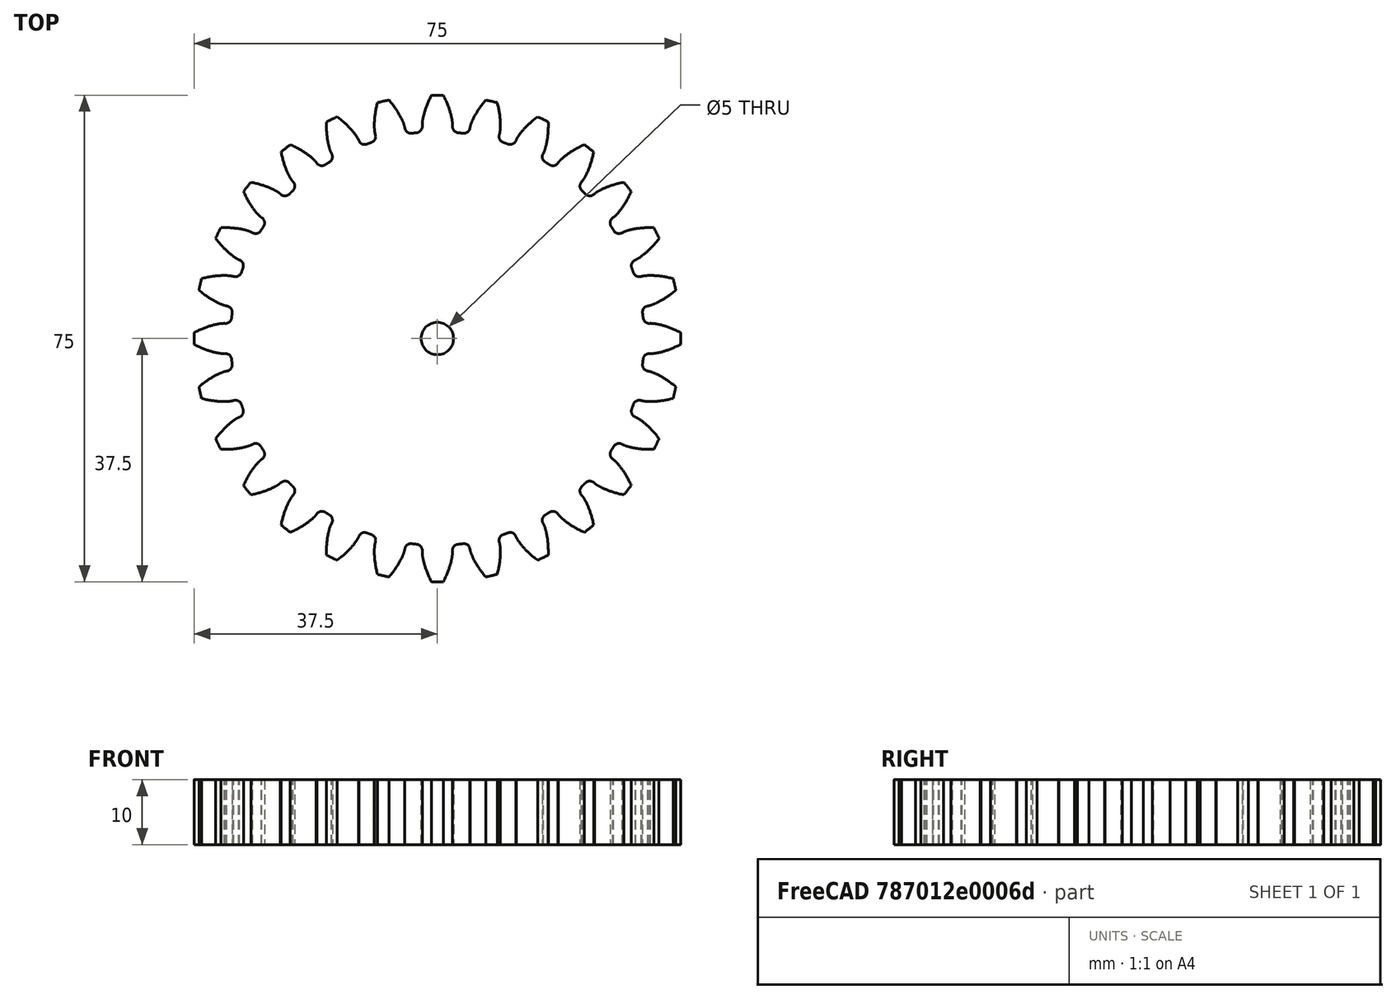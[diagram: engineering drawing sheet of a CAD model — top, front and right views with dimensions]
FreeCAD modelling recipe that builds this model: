
FCSTD DOCUMENT  (FreeCAD 1.0R39109 (Git))
Label: ギヤ70mm
License: All rights reserved
LicenseURL: https://en.wikipedia.org/wiki/All_rights_reserved
objects: Part::Part2DObjectPython×1, PartDesign::Pad×1, Sketcher::SketchObject×1, PartDesign::Pocket×1, PartDesign::Body×1
note: 10 computed .brp shape members not serialized (recipe doc carries the construction recipe); baked Part::Feature solids carry a one-line shape summary decoded from their .brp

FEATURE [Part::Part2DObjectPython] InvoluteGear  # Draft 2D object (typed FeaturePython)
  AddendumCoefficient = 1
  DedendumCoefficient = 1.25
  ExternalGear = true
  HighPrecision = true
  Modules = 2.5
  NumberOfTeeth = 28
  PressureAngle = 20
  ProfileShiftCoefficient = 0
  RootFilletCoefficient = 0.38
FEATURE [PartDesign::Pad] Pad
  Direction = (0,0,1)
  Length = 10
  Length2 = 10
  Profile = -> InvoluteGear
  ReferenceAxis = -> InvoluteGear [N_Axis]
  Refine = true
  Suppressed = false
  Type = 0
FEATURE [Sketcher::SketchObject] Sketch
  ArcFitTolerance = 1e-06
  AttachmentSupport = -> [Pad]
  FullyConstrained = true
  MakeInternals = false
  MapMode = 5
  Placement = pos=(0,0,10) rot=(0,0,1;0rad)
  sketch-geometry (1):
    g0: Circle CenterX=0 CenterY=0 CenterZ=0 NormalX=0 NormalY=0 NormalZ=1 AngleXU=0 Radius=2.5
  constraints (2):
    c: Coincident(g0,g-1)
    c: Diameter(g0) = 5
FEATURE [PartDesign::Pocket] Pocket
  BaseFeature = -> Pad
  Direction = (0,0,-1)
  Length = 5
  Length2 = 5
  Profile = -> Sketch
  ReferenceAxis = -> Sketch [N_Axis]
  Refine = true
  Suppressed = false
  Type = 1
FEATURE [PartDesign::Body] Body
  AllowCompound = false
  Group = -> [InvoluteGear,Pad,Sketch,Pocket]
  Origin = -> Origin
  Tip = -> Pocket
